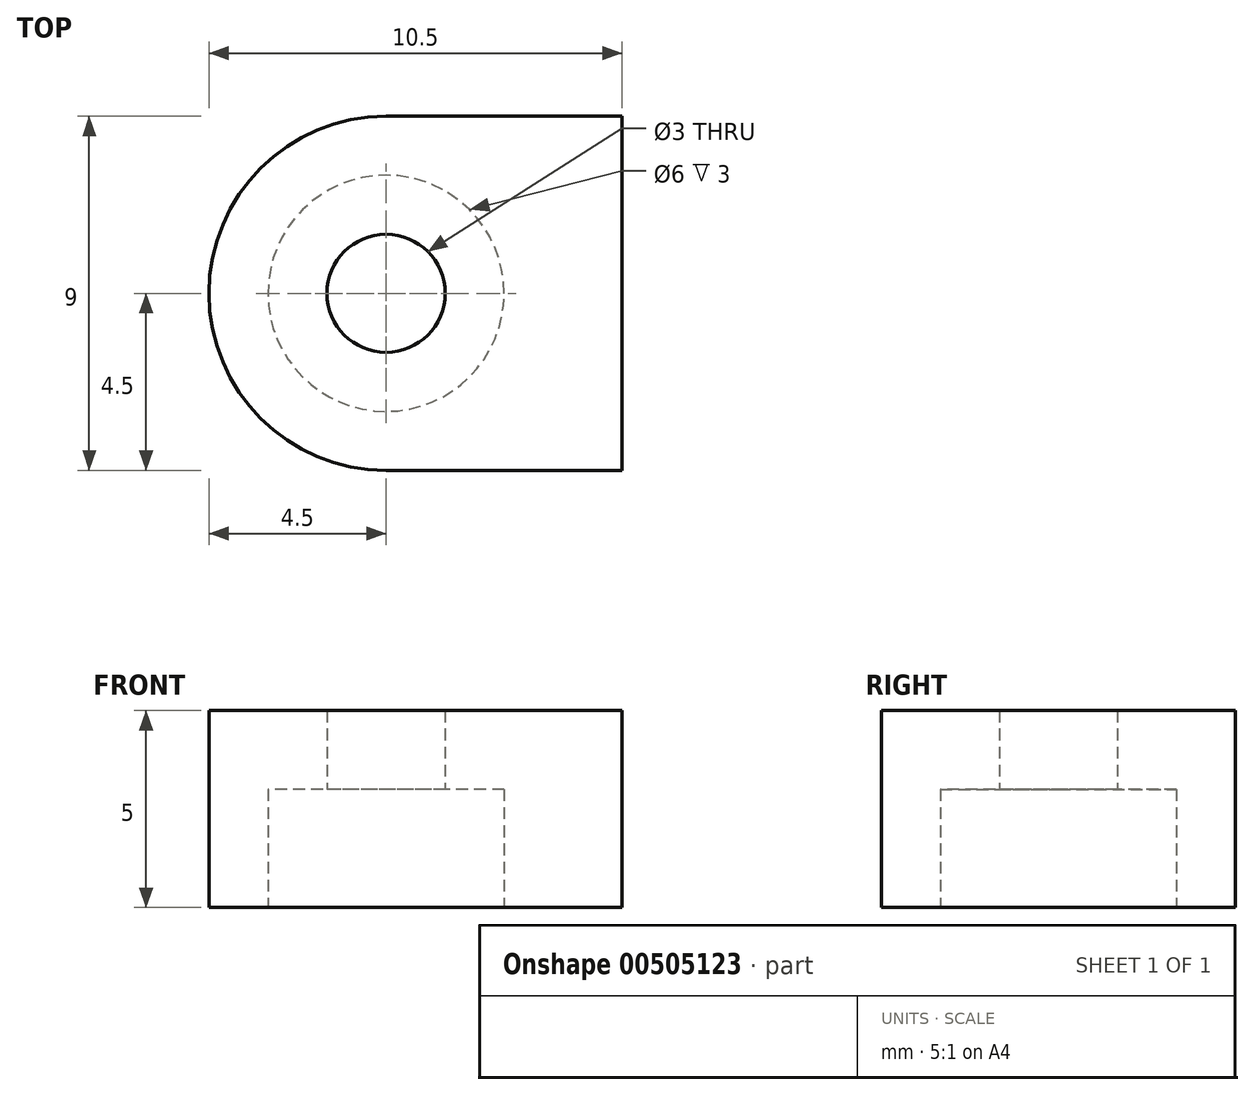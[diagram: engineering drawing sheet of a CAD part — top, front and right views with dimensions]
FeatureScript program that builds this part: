
annotation { "Feature Type Name" : "Feature", "Feature Type Description" : "" }
export const myFeature = defineFeature(function(context is Context, id is Id, definition is map)
    precondition{}
    {
        {
            var Q0;
            Q0=qCreatedBy(makeId("Top.planeOp"),FACE);
            var sketch = newSketch(context, id + "F0", { "sketchPlane" : qUnion([Q0])});
            skCircle(sketch, "E0", {"center": v(0, 0) * mm, "radius": 4.5 * mm});
            skLineSegment(sketch, "E1", {"start": v(0, 4.5) * mm, "end": v(6, 4.5) * mm});
            skLineSegment(sketch, "E2", {"start": v(6, 4.5) * mm, "end": v(6, -4.5) * mm});
            skLineSegment(sketch, "E3", {"start": v(6, -4.5) * mm, "end": v(0, -4.5) * mm});
            skSolve(sketch);
        }
        {
            var Q0;
            {var subQ0=sQuery(id+"F0.wireOp",EDGE,"E1");Q0=makeQuery(id+"F0.imprint","IMPRINT",FACE,{"disambiguationData":[TD([[makeQuery(id+"F0.imprint","IMPRINT",EDGE,{"derivedFrom":subQ0}),-1.0]])]});}
            var Q1;
            {var subQ0=sQuery(id+"F0.wireOp",EDGE,"E0");var subQ1=makeQuery(id+"F0.imprint","INTERSECT",VERTEX,{"derivedFrom":[subQ0,sQuery(id+"F0.wireOp",EDGE,"E1")]});Q1=makeQuery(id+"F0.imprint","IMPRINT",FACE,{"disambiguationData":[TD([[makeQuery(id+"F0.imprint","IMPRINT",EDGE,{"disambiguationData":[TD([[subQ1,-1.0]])],"derivedFrom":subQ0}),1.0]])]});}
            extrude(context, id + "F1", {"entities" : qUnion([Q0, Q1]), "depth" : 5 * mm, "offsetDistance" : 25 * mm});
        }
        {
            var Q0;
            Q0=qCreatedBy(makeId("Top.planeOp"),FACE);
            var sketch = newSketch(context, id + "F2", { "sketchPlane" : qUnion([Q0])});
            skCircle(sketch, "E4", {"center": v(0, 0) * mm, "radius": 1.5 * mm});
            skSolve(sketch);
        }
        {
            var Q0;
            Q0 = qSketchRegion(id + "F2", true);
            extrude(context, id + "F3", {"entities" : qUnion([Q0]), "operationType" : NewBodyOperationType.REMOVE, "depth" : 18.5 * mm});
        }
        {
            var Q0;
            Q0=qCreatedBy(makeId("Top.planeOp"),FACE);
            var sketch = newSketch(context, id + "F4", { "sketchPlane" : qUnion([Q0])});
            skCircle(sketch, "E5", {"center": v(0, 0) * mm, "radius": 3 * mm});
            skSolve(sketch);
        }
        {
            var Q0;
            Q0 = qSketchRegion(id + "F4", true);
            extrude(context, id + "F5", {"entities" : qUnion([Q0]), "operationType" : NewBodyOperationType.REMOVE, "depth" : 3 * mm});
        }
    });
